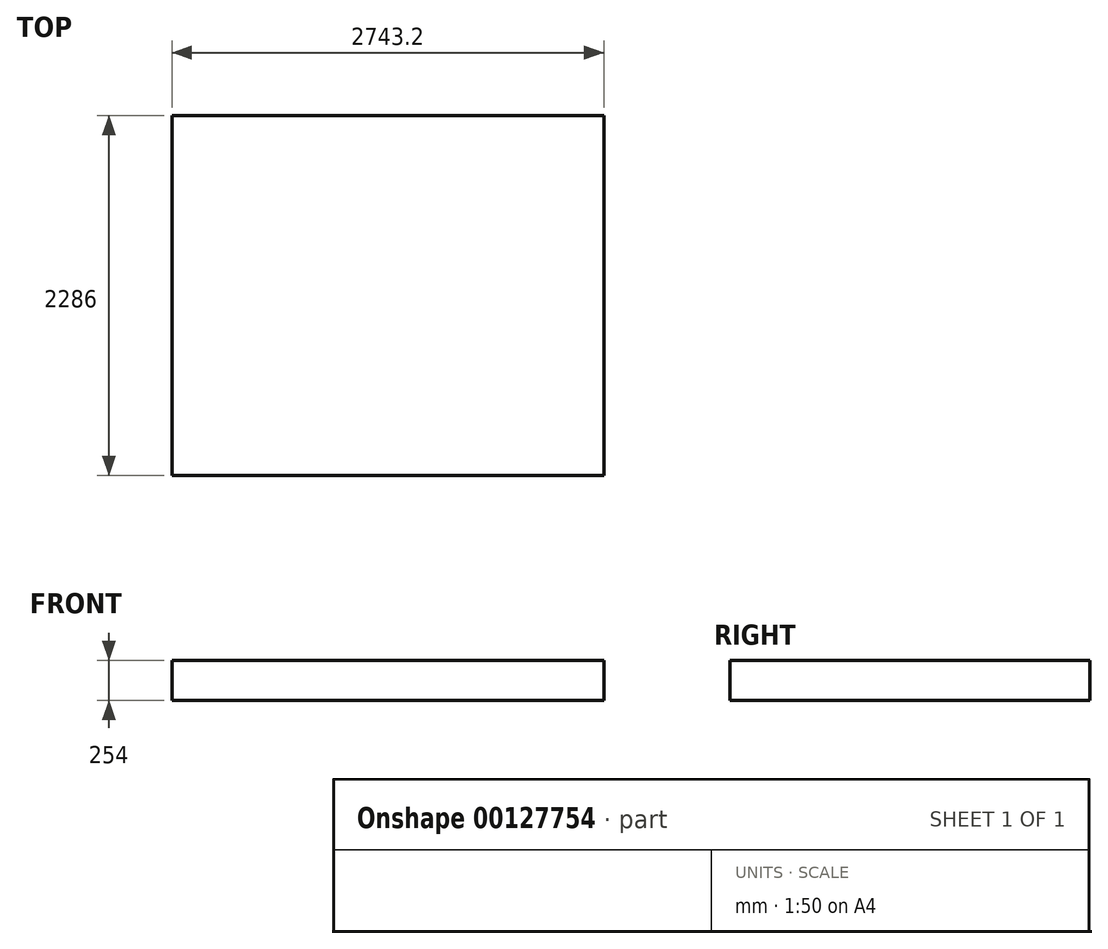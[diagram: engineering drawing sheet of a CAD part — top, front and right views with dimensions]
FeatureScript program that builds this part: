
annotation { "Feature Type Name" : "Feature", "Feature Type Description" : "" }
export const myFeature = defineFeature(function(context is Context, id is Id, definition is map)
    precondition{}
    {
        {
            var Q0;
            Q0=qCreatedBy(makeId("Top.planeOp"),FACE);
            var sketch = newSketch(context, id + "F0", { "sketchPlane" : qUnion([Q0])});
            skLineSegment(sketch, "E0.bottom", {"start": v(2743.2, -2286) * mm, "end": v(0, -2286) * mm});
            skLineSegment(sketch, "E0.top", {"start": v(2743.2, 0) * mm, "end": v(0, 0) * mm});
            skLineSegment(sketch, "E0.left", {"start": v(2743.2, -2286) * mm, "end": v(2743.2, 0) * mm});
            skLineSegment(sketch, "E0.right", {"start": v(0, -2286) * mm, "end": v(0, 0) * mm});
            skSolve(sketch);
        }
        {
            var Q0;
            Q0 = qSketchRegion(id + "F0", true);
            extrude(context, id + "F1", {"entities" : qUnion([Q0]), "oppositeDirection" : true, "depth" : 254 * mm});
        }
    });
